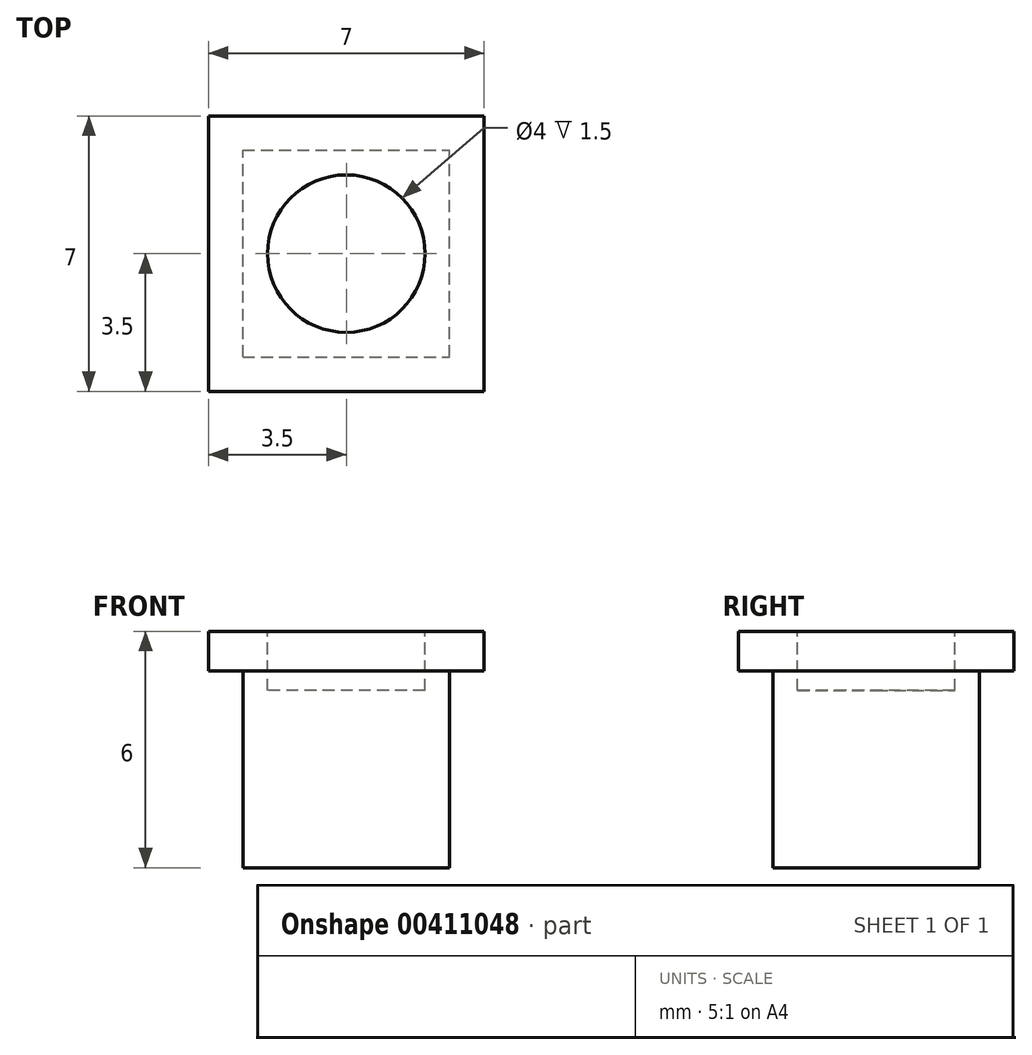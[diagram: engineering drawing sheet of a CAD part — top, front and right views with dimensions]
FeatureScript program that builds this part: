
annotation { "Feature Type Name" : "Feature", "Feature Type Description" : "" }
export const myFeature = defineFeature(function(context is Context, id is Id, definition is map)
    precondition{}
    {
        {
            var Q0;
            Q0=qCreatedBy(makeId("Top.planeOp"),FACE);
            var sketch = newSketch(context, id + "F0", { "sketchPlane" : qUnion([Q0])});
            skLineSegment(sketch, "E0.bottom", {"start": v(-2.62, -2.62) * mm, "end": v(2.63, -2.62) * mm});
            skLineSegment(sketch, "E0.top", {"start": v(-2.63, 2.62) * mm, "end": v(2.62, 2.62) * mm});
            skLineSegment(sketch, "E0.left", {"start": v(-2.62, -2.62) * mm, "end": v(-2.63, 2.62) * mm});
            skLineSegment(sketch, "E0.right", {"start": v(2.63, -2.62) * mm, "end": v(2.62, 2.62) * mm});
            skPoint(sketch, "E0.middle", {"position": v(0, 0) * mm});
            skSolve(sketch);
        }
        {
            var Q0;
            Q0 = qSketchRegion(id + "F0", true);
            extrude(context, id + "F1", {"entities" : qUnion([Q0]), "depth" : 5 * mm});
        }
        {
            var Q0;
            Q0=makeQuery(id+"F1.opExtrude","CAP_FACE",FACE,{"disambiguationData":[OSD([sQuery(id+"F0.wireOp",EDGE,"E0.bottom"),sQuery(id+"F0.wireOp",EDGE,"E0.top"),sQuery(id+"F0.wireOp",EDGE,"E0.left"),sQuery(id+"F0.wireOp",EDGE,"E0.right")])],"isStart":false});
            var sketch = newSketch(context, id + "F2", { "sketchPlane" : qUnion([Q0])});
            skLineSegment(sketch, "E1.bottom", {"start": v(-3.5, -3.5) * mm, "end": v(3.5, -3.5) * mm});
            skLineSegment(sketch, "E1.top", {"start": v(-3.5, 3.5) * mm, "end": v(3.5, 3.5) * mm});
            skLineSegment(sketch, "E1.left", {"start": v(-3.5, -3.5) * mm, "end": v(-3.5, 3.5) * mm});
            skLineSegment(sketch, "E1.right", {"start": v(3.5, -3.5) * mm, "end": v(3.5, 3.5) * mm});
            skPoint(sketch, "E1.middle", {"position": v(0, 0) * mm});
            skSolve(sketch);
        }
        {
            var Q0;
            Q0 = qSketchRegion(id + "F2", true);
            extrude(context, id + "F3", {"entities" : qUnion([Q0]), "operationType" : NewBodyOperationType.ADD, "depth" : 1 * mm});
        }
        {
            var Q0;
            Q0=makeQuery(id+"F3.opExtrude","CAP_FACE",FACE,{"disambiguationData":[OSD([sQuery(id+"F2.wireOp",EDGE,"E1.bottom"),sQuery(id+"F2.wireOp",EDGE,"E1.top"),sQuery(id+"F2.wireOp",EDGE,"E1.left"),sQuery(id+"F2.wireOp",EDGE,"E1.right")])],"isStart":false});
            var sketch = newSketch(context, id + "F4", { "sketchPlane" : qUnion([Q0])});
            skCircle(sketch, "E2", {"center": v(0, 0) * mm, "radius": 2 * mm});
            skSolve(sketch);
        }
        {
            var Q0;
            Q0 = qSketchRegion(id + "F4", true);
            extrude(context, id + "F5", {"entities" : qUnion([Q0]), "operationType" : NewBodyOperationType.REMOVE, "oppositeDirection" : true, "depth" : 1.5 * mm});
        }
    });
